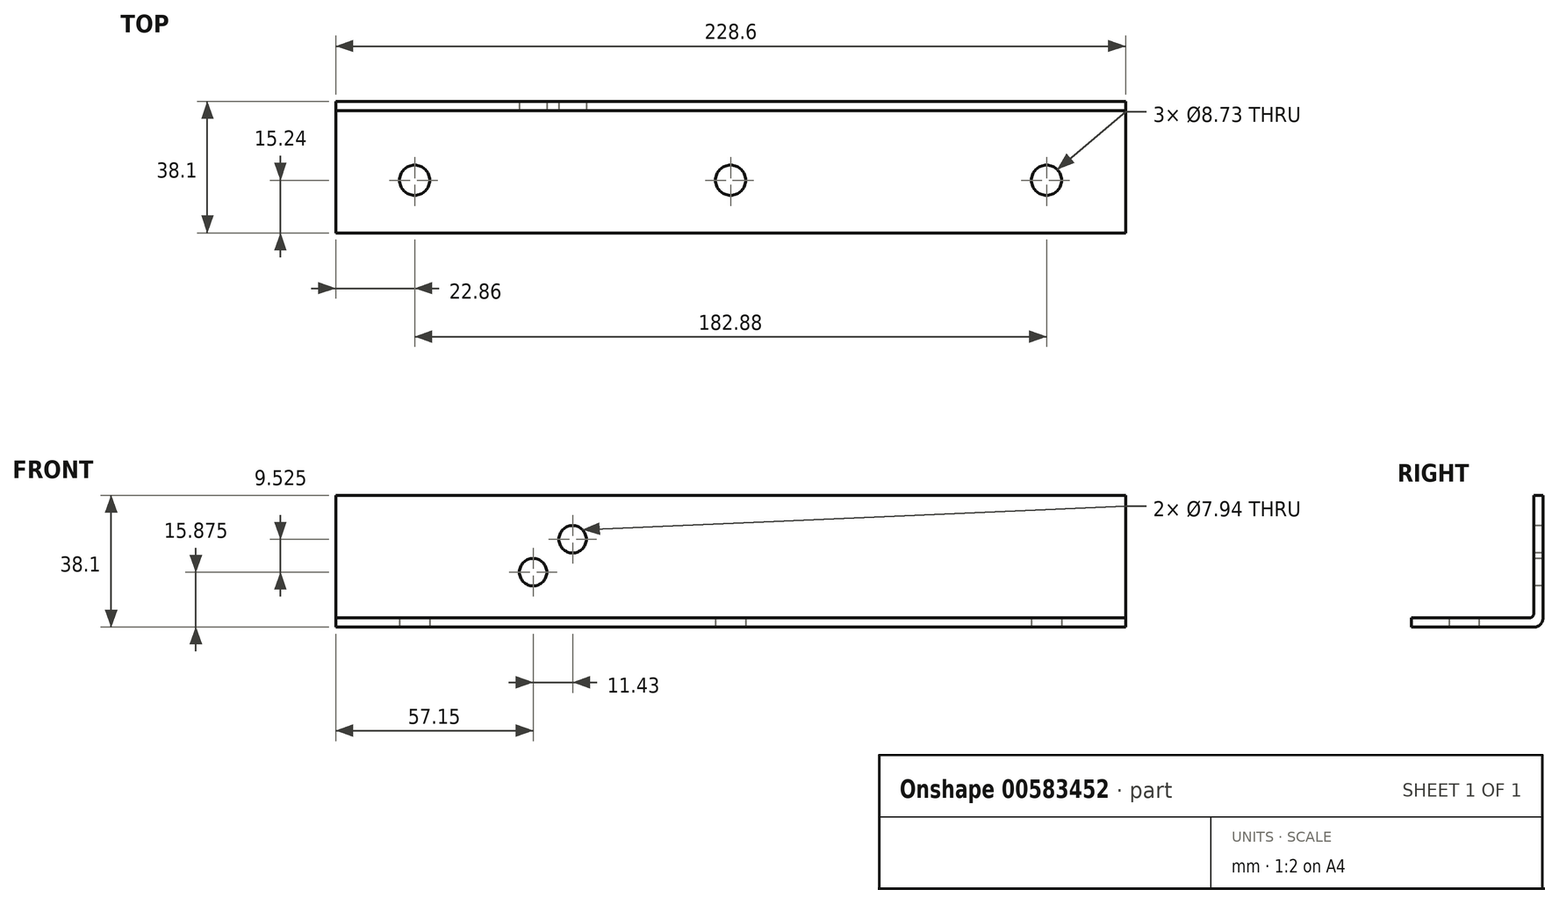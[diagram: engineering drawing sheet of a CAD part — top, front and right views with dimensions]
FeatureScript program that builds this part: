
annotation { "Feature Type Name" : "Feature", "Feature Type Description" : "" }
export const myFeature = defineFeature(function(context is Context, id is Id, definition is map)
    precondition{}
    {
        {
            var Q0;
            Q0=qCreatedBy(makeId("Front.planeOp"),FACE);
            var sketch = newSketch(context, id + "F0", { "sketchPlane" : qUnion([Q0])});
            skLineSegment(sketch, "E0.bottom", {"start": v(114.3, -19.05) * mm, "end": v(-114.3, -19.05) * mm});
            skLineSegment(sketch, "E0.top", {"start": v(114.3, 19.05) * mm, "end": v(-114.3, 19.05) * mm});
            skLineSegment(sketch, "E0.left", {"start": v(114.3, -19.05) * mm, "end": v(114.3, 19.05) * mm});
            skLineSegment(sketch, "E0.right", {"start": v(-114.3, -19.05) * mm, "end": v(-114.3, 19.05) * mm});
            skPoint(sketch, "E0.middle", {"position": v(0, 0) * mm});
            skSolve(sketch);
        }
        {
            var Q0;
            Q0=qSketchRegion(id+"F0",true);
            extrude(context, id + "F1", {"entities" : qUnion([Q0]), "depth" : 2.66 * mm});
        }
        {
            var Q0;
            Q0=makeQuery(id+"F1.opExtrude","SWEPT_FACE",FACE,{"disambiguationData":[OSD([sQuery(id+"F0.wireOp",EDGE,"E0.bottom")])]});
            var sketch = newSketch(context, id + "F2", { "sketchPlane" : qUnion([Q0])});
            skLineSegment(sketch, "E1.bottom", {"start": v(-114.3, 0) * mm, "end": v(114.3, 0) * mm});
            skLineSegment(sketch, "E1.top", {"start": v(-114.3, 38.1) * mm, "end": v(114.3, 38.1) * mm});
            skLineSegment(sketch, "E1.left", {"start": v(-114.3, 0) * mm, "end": v(-114.3, 38.1) * mm});
            skLineSegment(sketch, "E1.right", {"start": v(114.3, 0) * mm, "end": v(114.3, 38.1) * mm});
            skSolve(sketch);
        }
        {
            var Q0;
            Q0=qSketchRegion(id+"F2",true);
            extrude(context, id + "F3", {"entities" : qUnion([Q0]), "operationType" : NewBodyOperationType.ADD, "oppositeDirection" : true, "depth" : 2.66 * mm});
        }
        {
            var Q0;
            Q0=makeQuery(id+"F1.opExtrude","CAP_FACE",FACE,{"disambiguationData":[OSD([sQuery(id+"F0.wireOp",EDGE,"E0.bottom"),sQuery(id+"F0.wireOp",EDGE,"E0.top"),sQuery(id+"F0.wireOp",EDGE,"E0.left"),sQuery(id+"F0.wireOp",EDGE,"E0.right")])],"isStart":false});
            var sketch = newSketch(context, id + "F4", { "sketchPlane" : qUnion([Q0])});
            skCircle(sketch, "E2", {"center": v(-45.72, 6.35) * mm, "radius": 3.97 * mm});
            skCircle(sketch, "E3", {"center": v(-57.15, -3.18) * mm, "radius": 3.97 * mm});
            skSolve(sketch);
        }
        {
            var Q0;
            Q0=qSketchRegion(id+"F4",true);
            extrude(context, id + "F5", {"entities" : qUnion([Q0]), "operationType" : NewBodyOperationType.REMOVE, "oppositeDirection" : true, "depth" : 2.66 * mm});
        }
        {
            var Q0;
            Q0=makeQuery(id+"F3.boolean.opBoolean","MERGE",FACE,{"derivedFrom":[makeQuery(id+"F1.opExtrude","SWEPT_FACE",FACE,{"disambiguationData":[OSD([sQuery(id+"F0.wireOp",EDGE,"E0.bottom")])]}),makeQuery(id+"F3.opExtrude","CAP_FACE",FACE,{"disambiguationData":[OSD([sQuery(id+"F2.wireOp",EDGE,"E1.bottom"),sQuery(id+"F2.wireOp",EDGE,"E1.top"),sQuery(id+"F2.wireOp",EDGE,"E1.left"),sQuery(id+"F2.wireOp",EDGE,"E1.right")])],"isStart":true})]});
            var sketch = newSketch(context, id + "F6", { "sketchPlane" : qUnion([Q0])});
            skCircle(sketch, "E4", {"center": v(-91.44, 22.86) * mm, "radius": 4.37 * mm});
            skCircle(sketch, "E5", {"center": v(0, 22.86) * mm, "radius": 4.37 * mm});
            skCircle(sketch, "E6", {"center": v(91.44, 22.86) * mm, "radius": 4.37 * mm});
            skSolve(sketch);
        }
        {
            var Q0;
            Q0=qSketchRegion(id+"F6",true);
            extrude(context, id + "F7", {"entities" : qUnion([Q0]), "operationType" : NewBodyOperationType.REMOVE, "oppositeDirection" : true, "depth" : 2.66 * mm});
        }
        {
            var Q0;
            Q0=makeQuery(id+"F1.opExtrude","CAP_EDGE",EDGE,{"disambiguationData":[OSD([sQuery(id+"F0.wireOp",EDGE,"E0.bottom")])],"isStart":true});
            fillet(context, id + "F8", {"entities" : qUnion([Q0]), "radius" : 2.54 * mm, "tangentPropagation" : true, "allowEdgeOverflow" : false});
        }
        {
            var Q0;
            Q0=makeQuery(id+"F3.boolean.opBoolean","INTERSECT",EDGE,{"derivedFrom":[makeQuery(id+"F1.opExtrude","CAP_FACE",FACE,{"disambiguationData":[OSD([sQuery(id+"F0.wireOp",EDGE,"E0.bottom"),sQuery(id+"F0.wireOp",EDGE,"E0.top"),sQuery(id+"F0.wireOp",EDGE,"E0.left"),sQuery(id+"F0.wireOp",EDGE,"E0.right")])],"isStart":false}),makeQuery(id+"F3.opExtrude","CAP_FACE",FACE,{"disambiguationData":[OSD([sQuery(id+"F2.wireOp",EDGE,"E1.bottom"),sQuery(id+"F2.wireOp",EDGE,"E1.top"),sQuery(id+"F2.wireOp",EDGE,"E1.left"),sQuery(id+"F2.wireOp",EDGE,"E1.right")])],"isStart":false})]});
            fillet(context, id + "F9", {"entities" : qUnion([Q0]), "radius" : 1.27 * mm, "tangentPropagation" : true, "allowEdgeOverflow" : false});
        }
    });
